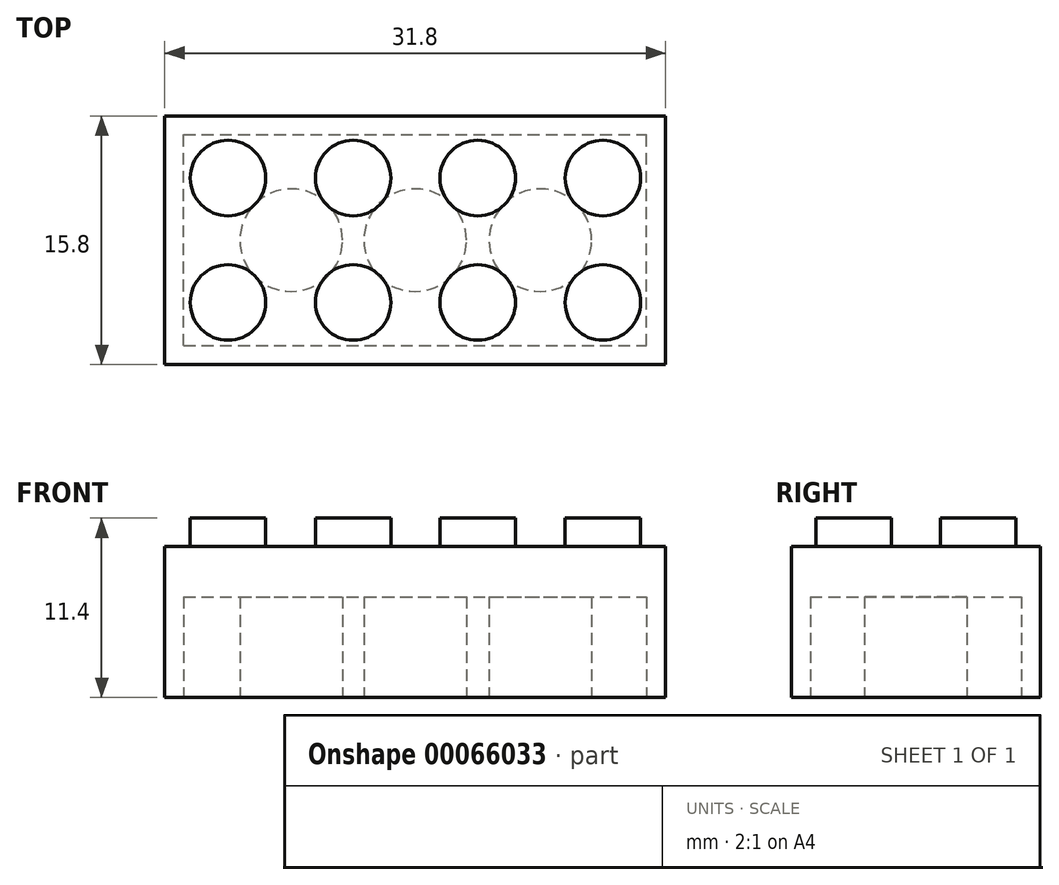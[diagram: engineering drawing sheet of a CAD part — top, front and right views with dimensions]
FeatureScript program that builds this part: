
annotation { "Feature Type Name" : "Feature", "Feature Type Description" : "" }
export const myFeature = defineFeature(function(context is Context, id is Id, definition is map)
    precondition{}
    {
        {
            var Q0;
            Q0=qCreatedBy(makeId("Front.planeOp"),FACE);
            var sketch = newSketch(context, id + "F0", { "sketchPlane" : qUnion([Q0])});
            skLineSegment(sketch, "E0.bottom", {"start": v(-8.03, -9.6) * mm, "end": v(23.77, -9.6) * mm});
            skLineSegment(sketch, "E0.top", {"start": v(-8.03, 0) * mm, "end": v(23.77, 0) * mm});
            skLineSegment(sketch, "E0.left", {"start": v(-8.03, -9.6) * mm, "end": v(-8.03, 0) * mm});
            skLineSegment(sketch, "E0.right", {"start": v(23.77, -9.6) * mm, "end": v(23.77, 0) * mm});
            skSolve(sketch);
        }
        {
            var Q0;
            Q0=makeQuery(id+"F0.imprint","IMPRINT",FACE,{"disambiguationData":[TD([[makeQuery(id+"F0.imprint","IMPRINT",EDGE,{"derivedFrom":sQuery(id+"F0.wireOp",EDGE,"E0.bottom")}),1.0]])]});
            extrude(context, id + "F1", {"entities" : qUnion([Q0]), "depth" : 15.8 * mm});
        }
        {
            var Q0;
            Q0=makeQuery(id+"F1.opExtrude","SWEPT_FACE",FACE,{"disambiguationData":[OSD([sQuery(id+"F0.wireOp",EDGE,"E0.top")])]});
            var sketch = newSketch(context, id + "F2", { "sketchPlane" : qUnion([Q0])});
            skLineSegment(sketch, "E1", {"start": v(7.87, 0) * mm, "end": v(7.87, -15.8) * mm});
            skLineSegment(sketch, "E2", {"start": v(23.77, -7.9) * mm, "end": v(-8.03, -7.9) * mm});
            skCircle(sketch, "E3", {"center": v(-4.02, -3.95) * mm, "radius": 2.4 * mm});
            skCircle(sketch, "E4", {"center": v(-4.02, -11.85) * mm, "radius": 2.4 * mm});
            skCircle(sketch, "E5", {"center": v(3.93, -3.95) * mm, "radius": 2.4 * mm});
            skCircle(sketch, "E6", {"center": v(3.93, -11.85) * mm, "radius": 2.4 * mm});
            skCircle(sketch, "E7", {"center": v(11.84, -3.95) * mm, "radius": 2.4 * mm});
            skCircle(sketch, "E8", {"center": v(19.8, -3.95) * mm, "radius": 2.4 * mm});
            skCircle(sketch, "E9", {"center": v(11.84, -11.85) * mm, "radius": 2.4 * mm});
            skCircle(sketch, "E10", {"center": v(19.8, -11.85) * mm, "radius": 2.4 * mm});
            skSolve(sketch);
        }
        {
            var Q0;
            Q0=makeQuery(id+"F2.imprint","IMPRINT",FACE,{"disambiguationData":[TD([[makeQuery(id+"F2.imprint","IMPRINT",EDGE,{"derivedFrom":sQuery(id+"F2.wireOp",EDGE,"E8")}),1.0]])]});
            var Q1;
            Q1=makeQuery(id+"F2.imprint","IMPRINT",FACE,{"disambiguationData":[TD([[makeQuery(id+"F2.imprint","IMPRINT",EDGE,{"derivedFrom":sQuery(id+"F2.wireOp",EDGE,"E10")}),1.0]])]});
            var Q2;
            Q2=makeQuery(id+"F2.imprint","IMPRINT",FACE,{"disambiguationData":[TD([[makeQuery(id+"F2.imprint","IMPRINT",EDGE,{"derivedFrom":sQuery(id+"F2.wireOp",EDGE,"E9")}),1.0]])]});
            var Q3;
            Q3=makeQuery(id+"F2.imprint","IMPRINT",FACE,{"disambiguationData":[TD([[makeQuery(id+"F2.imprint","IMPRINT",EDGE,{"derivedFrom":sQuery(id+"F2.wireOp",EDGE,"E5")}),1.0]])]});
            var Q4;
            Q4=makeQuery(id+"F2.imprint","IMPRINT",FACE,{"disambiguationData":[TD([[makeQuery(id+"F2.imprint","IMPRINT",EDGE,{"derivedFrom":sQuery(id+"F2.wireOp",EDGE,"E7")}),1.0]])]});
            var Q5;
            Q5=makeQuery(id+"F2.imprint","IMPRINT",FACE,{"disambiguationData":[TD([[makeQuery(id+"F2.imprint","IMPRINT",EDGE,{"derivedFrom":sQuery(id+"F2.wireOp",EDGE,"E6")}),1.0]])]});
            var Q6;
            Q6=makeQuery(id+"F2.imprint","IMPRINT",FACE,{"disambiguationData":[TD([[makeQuery(id+"F2.imprint","IMPRINT",EDGE,{"derivedFrom":sQuery(id+"F2.wireOp",EDGE,"E4")}),1.0]])]});
            var Q7;
            Q7=makeQuery(id+"F2.imprint","IMPRINT",FACE,{"disambiguationData":[TD([[makeQuery(id+"F2.imprint","IMPRINT",EDGE,{"derivedFrom":sQuery(id+"F2.wireOp",EDGE,"E3")}),1.0]])]});
            var Q8;
            Q8=sQuery(id+"F2.wireOp",EDGE,"E3");
            extrude(context, id + "F3", {"entities" : qUnion([Q0, Q1, Q2, Q3, Q4, Q5, Q6, Q7]), "surfaceEntities" : qUnion([Q8]), "depth" : 1.8 * mm});
        }
        {
            var Q0;
            Q0=makeQuery(id+"F1.opExtrude","SWEPT_FACE",FACE,{"disambiguationData":[OSD([sQuery(id+"F0.wireOp",EDGE,"E0.bottom")])]});
            var sketch = newSketch(context, id + "F4", { "sketchPlane" : qUnion([Q0])});
            skCircle(sketch, "E11", {"center": v(7.87, 7.9) * mm, "radius": 2.4 * mm});
            skCircle(sketch, "E12", {"center": v(0, 7.9) * mm, "radius": 2.4 * mm});
            skCircle(sketch, "E13", {"center": v(15.82, 7.9) * mm, "radius": 2.4 * mm});
            skCircle(sketch, "E14", {"center": v(15.82, 7.9) * mm, "radius": 3.26 * mm});
            skCircle(sketch, "E15", {"center": v(7.87, 7.9) * mm, "radius": 3.26 * mm});
            skCircle(sketch, "E16", {"center": v(0, 7.9) * mm, "radius": 3.26 * mm});
            skLineSegment(sketch, "E17.bottom", {"start": v(-6.83, 14.6) * mm, "end": v(22.57, 14.6) * mm});
            skLineSegment(sketch, "E17.top", {"start": v(-6.83, 1.2) * mm, "end": v(22.57, 1.2) * mm});
            skLineSegment(sketch, "E17.left", {"start": v(-6.83, 14.6) * mm, "end": v(-6.83, 1.2) * mm});
            skLineSegment(sketch, "E17.right", {"start": v(22.57, 14.6) * mm, "end": v(22.57, 1.2) * mm});
            skSolve(sketch);
        }
        {
            var Q0;
            Q0=makeQuery(id+"F4.imprint","IMPRINT",FACE,{"disambiguationData":[TD([[makeQuery(id+"F4.imprint","IMPRINT",EDGE,{"derivedFrom":sQuery(id+"F4.wireOp",EDGE,"E14")}),-1.0]])]});
            extrude(context, id + "F5", {"entities" : qUnion([Q0]), "operationType" : NewBodyOperationType.REMOVE, "oppositeDirection" : true, "depth" : 6.4 * mm});
        }
        {
            var Q0;
            Q0=sQuery(id+"F4.wireOp",EDGE,"E13");
            var Q1;
            Q1=sQuery(id+"F4.wireOp",EDGE,"E11");
            var Q2;
            Q2=sQuery(id+"F4.wireOp",EDGE,"E12");
            extrude(context, id + "F6", {"bodyType" : ToolBodyType.SURFACE, "operationType" : NewBodyOperationType.REMOVE, "surfaceEntities" : qUnion([Q0, Q1, Q2]), "oppositeDirection" : true, "depth" : 6.4 * mm});
        }
    });
